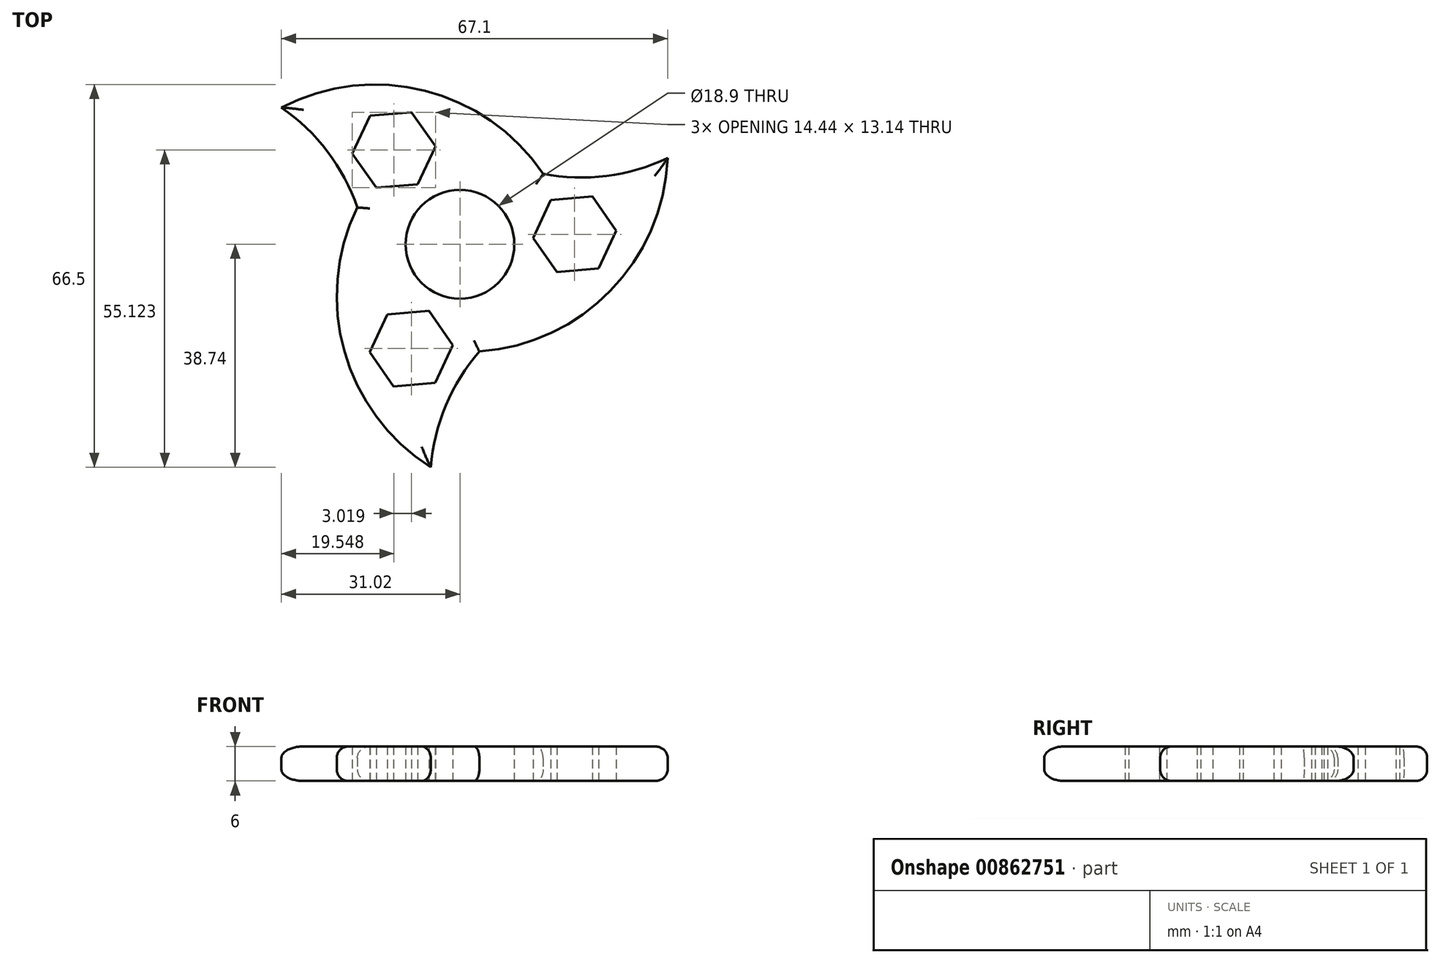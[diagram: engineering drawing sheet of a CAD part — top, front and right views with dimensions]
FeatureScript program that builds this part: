
annotation { "Feature Type Name" : "Feature", "Feature Type Description" : "" }
export const myFeature = defineFeature(function(context is Context, id is Id, definition is map)
    precondition{}
    {
        {
            var Q0;
            Q0=qCreatedBy(makeId("Top.planeOp"),FACE);
            var sketch = newSketch(context, id + "F0", { "sketchPlane" : qUnion([Q0])});
            skCircle(sketch, "E0", {"center": v(0, 0) * mm, "radius": 9.45 * mm});
            skPoint(sketch, "E1", {"position": v(0, 18.7) * mm});
            skPoint(sketch, "E2.MirrorP", {"position": v(0, -18.7) * mm});
            skArc(sketch, "E3", {"start": v(0, 18.7) * mm, "mid": v(17.52, 11.78) * mm, "end": v(36.08, 14.98) * mm});
            skArc(sketch, "E4", {"start": v(0, -18.7) * mm, "mid": v(24.95, -9.25) * mm, "end": v(36.08, 14.98) * mm});
            skArc(sketch, "E5.1.0", {"start": v(-16.19, -9.35) * mm, "mid": v(-18.96, 9.29) * mm, "end": v(-31.02, 23.76) * mm});
            skArc(sketch, "E5.1.1", {"start": v(16.19, 9.35) * mm, "mid": v(-4.46, 26.23) * mm, "end": v(-31.02, 23.76) * mm});
            skArc(sketch, "E5.2.0", {"start": v(16.19, -9.35) * mm, "mid": v(1.44, -21.06) * mm, "end": v(-5.07, -38.74) * mm});
            skArc(sketch, "E5.2.1", {"start": v(-16.19, 9.35) * mm, "mid": v(-20.49, -16.98) * mm, "end": v(-5.07, -38.74) * mm});
            skLineSegment(sketch, "E6", {"start": v(0, 0) * mm, "end": v(19.92, 1.74) * mm, "construction": true});
            skCircle(sketch, "E7.cCircle", {"center": v(19.92, 1.74) * mm, "radius": 7.25 * mm, "construction": true});
            skLineSegment(sketch, "E7.0", {"start": v(12.7, 1.11) * mm, "end": v(15.77, 7.68) * mm});
            skLineSegment(sketch, "E7.1", {"start": v(15.77, 7.68) * mm, "end": v(22.99, 8.31) * mm});
            skLineSegment(sketch, "E7.2", {"start": v(22.99, 8.31) * mm, "end": v(27.15, 2.37) * mm});
            skLineSegment(sketch, "E7.3", {"start": v(27.15, 2.37) * mm, "end": v(24.08, -4.2) * mm});
            skLineSegment(sketch, "E7.4", {"start": v(24.08, -4.2) * mm, "end": v(16.86, -4.83) * mm});
            skLineSegment(sketch, "E7.5", {"start": v(16.86, -4.83) * mm, "end": v(12.7, 1.11) * mm});
            skLineSegment(sketch, "E8.1.0", {"start": v(-14.54, 9.81) * mm, "end": v(-18.7, 15.75) * mm});
            skLineSegment(sketch, "E8.1.1", {"start": v(-18.7, 15.75) * mm, "end": v(-15.63, 22.32) * mm});
            skLineSegment(sketch, "E8.1.2", {"start": v(-15.63, 22.32) * mm, "end": v(-8.4, 22.95) * mm});
            skLineSegment(sketch, "E8.1.3", {"start": v(-8.4, 22.95) * mm, "end": v(-4.25, 17.01) * mm});
            skLineSegment(sketch, "E8.1.4", {"start": v(-4.25, 17.01) * mm, "end": v(-7.31, 10.44) * mm});
            skLineSegment(sketch, "E8.1.5", {"start": v(-7.31, 10.44) * mm, "end": v(-14.54, 9.81) * mm});
            skLineSegment(sketch, "E8.2.0", {"start": v(-1.23, -17.5) * mm, "end": v(-4.3, -24.07) * mm});
            skLineSegment(sketch, "E8.2.1", {"start": v(-4.3, -24.07) * mm, "end": v(-11.52, -24.7) * mm});
            skLineSegment(sketch, "E8.2.2", {"start": v(-11.52, -24.7) * mm, "end": v(-15.67, -18.76) * mm});
            skLineSegment(sketch, "E8.2.3", {"start": v(-15.67, -18.76) * mm, "end": v(-12.61, -12.19) * mm});
            skLineSegment(sketch, "E8.2.4", {"start": v(-12.61, -12.19) * mm, "end": v(-5.39, -11.56) * mm});
            skLineSegment(sketch, "E8.2.5", {"start": v(-5.39, -11.56) * mm, "end": v(-1.23, -17.5) * mm});
            skSolve(sketch);
        }
        {
            var Q0;
            Q0=makeQuery(id+"F0.imprint","IMPRINT",FACE,{"disambiguationData":[TD([[makeQuery(id+"F0.imprint","IMPRINT",EDGE,{"derivedFrom":sQuery(id+"F0.wireOp",EDGE,"E0")}),-1.0]])]});
            extrude(context, id + "F1", {"entities" : qUnion([Q0]), "depth" : 6 * mm, "offsetDistance" : 25 * mm});
        }
        {
            var Q0;
            Q0=makeQuery(id+"F1.opExtrude","CAP_EDGE",EDGE,{"disambiguationData":[OSD([sQuery(id+"F0.wireOp",EDGE,"E5.1.0")])],"isStart":false});
            var Q1;
            Q1=makeQuery(id+"F1.opExtrude","CAP_EDGE",EDGE,{"disambiguationData":[OSD([sQuery(id+"F0.wireOp",EDGE,"E5.2.1")])],"isStart":false});
            var Q2;
            Q2=makeQuery(id+"F1.opExtrude","CAP_EDGE",EDGE,{"disambiguationData":[OSD([sQuery(id+"F0.wireOp",EDGE,"E5.2.0")])],"isStart":false});
            var Q3;
            Q3=makeQuery(id+"F1.opExtrude","CAP_EDGE",EDGE,{"disambiguationData":[OSD([sQuery(id+"F0.wireOp",EDGE,"E4")])],"isStart":false});
            var Q4;
            Q4=makeQuery(id+"F1.opExtrude","CAP_EDGE",EDGE,{"disambiguationData":[OSD([sQuery(id+"F0.wireOp",EDGE,"E3")])],"isStart":false});
            var Q5;
            Q5=makeQuery(id+"F1.opExtrude","CAP_EDGE",EDGE,{"disambiguationData":[OSD([sQuery(id+"F0.wireOp",EDGE,"E5.1.1")])],"isStart":false});
            var Q6;
            Q6=makeQuery(id+"F1.opExtrude","CAP_EDGE",EDGE,{"disambiguationData":[OSD([sQuery(id+"F0.wireOp",EDGE,"E5.1.1")])],"isStart":true});
            var Q7;
            Q7=makeQuery(id+"F1.opExtrude","CAP_EDGE",EDGE,{"disambiguationData":[OSD([sQuery(id+"F0.wireOp",EDGE,"E5.1.0")])],"isStart":true});
            var Q8;
            Q8=makeQuery(id+"F1.opExtrude","CAP_EDGE",EDGE,{"disambiguationData":[OSD([sQuery(id+"F0.wireOp",EDGE,"E5.2.1")])],"isStart":true});
            var Q9;
            Q9=makeQuery(id+"F1.opExtrude","CAP_EDGE",EDGE,{"disambiguationData":[OSD([sQuery(id+"F0.wireOp",EDGE,"E5.2.0")])],"isStart":true});
            var Q10;
            Q10=makeQuery(id+"F1.opExtrude","CAP_EDGE",EDGE,{"disambiguationData":[OSD([sQuery(id+"F0.wireOp",EDGE,"E4")])],"isStart":true});
            var Q11;
            Q11=makeQuery(id+"F1.opExtrude","CAP_EDGE",EDGE,{"disambiguationData":[OSD([sQuery(id+"F0.wireOp",EDGE,"E3")])],"isStart":true});
            fillet(context, id + "F2", {"entities" : qUnion([Q0, Q1, Q2, Q3, Q4, Q5, Q6, Q7, Q8, Q9, Q10, Q11]), "radius" : 2 * mm, "tangentPropagation" : true, "allowEdgeOverflow" : false});
        }
    });
